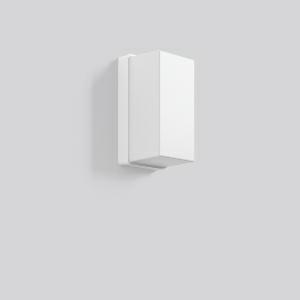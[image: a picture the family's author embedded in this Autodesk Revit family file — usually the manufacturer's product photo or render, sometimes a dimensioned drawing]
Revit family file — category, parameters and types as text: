
# Revit family: rechteck_221170_002_92ac
name_source: partatom
category: Lighting Fixtures
units: mm (PartAtom-declared; Revit-internal decimal feet)

## family parameters
Cut with Voids When Loaded = No
Host = Face
Light Source = No
Part Type = Normal
Room Calculation Point = No
Round Connector Dimension = Use Diameter
Shared = No

## types (1)
- RECHTECK (1 x LED Modul 830, 900 lm, 3000)
    Apparent Load = 9 VA
    CIE Flux Codes = 30 58 82 69 100
    Color Rendering = 80
    Color Temperature = 3000
    Default Elevation = 1800 mm
    Description = Series: RECHTECK
Rectangular surface-mounted luminaire in classic design. Base: plastic. Diffuser: plastic (polypropylene), opal, satin finish. Diffuser fastening: spring system. Suitable for Wall (surface). 
Colour: white
Length: 215 mm
Width: 115 mm
Height: 110 mm
Lamp: LED
Socket: without socket
Colour temperature: 3000K
Colour rendering index (CRI): 80
System power: 9 W
Rated luminous flux: 900 lm
Luminous efficiency: 100 lm/W
Control gear: Regulated power supply
Protection class: I
Type of protection: IP 44
    Height = 110 mm
    Lamp = 1 x LED Modul 830
    Lamp Light Flux = 900 lm
    Lamp count = 1
    Length = 215 mm
    Lifetime = 50000 h
    Luminous efficacy = 100 lm/W
    Manufacturer = RZB
    ModVariant = No
    Model = 221170.002
    Mounting Place = Wall, Ceiling
    Mounting Type = Surface mounted
    Number of Poles = 1
    OnlyDefault = Yes
    Power Factor = 1
    Product Name = RECHTECK
    Product group = Surface mounted ceiling and wall luminaires
    ProductGroupID = 305
    Protection Class = Protection class I
    Protection Degree = IP 44
    RLX_Detail_Level = 1
    RLX_Emergency_Light_Flux = 0 lm
    RLX_Emergency_Type = 0
    RLX_Emergency_Type_DB = No
    RlxData = <blob elided: 42429 chars, md5=da640e4f>
    Socket = socket
    Standby Power = 0 W
    System Light Flux = 900 lm
    System Power = 9 W
    Type Comments = Product without accessories
    Type Image = 22144.002.jpg
    URL = http://relux.com
    VarID = ---
    Voltage = 230 V
    Voltage Range = 220-240 V
    Weight = 0.00 kg
    Width = 115 mm

## geometry (parser evidence)
native form markers: Blend x4, Sweep x12
no freeform markers — native parametric forms only
